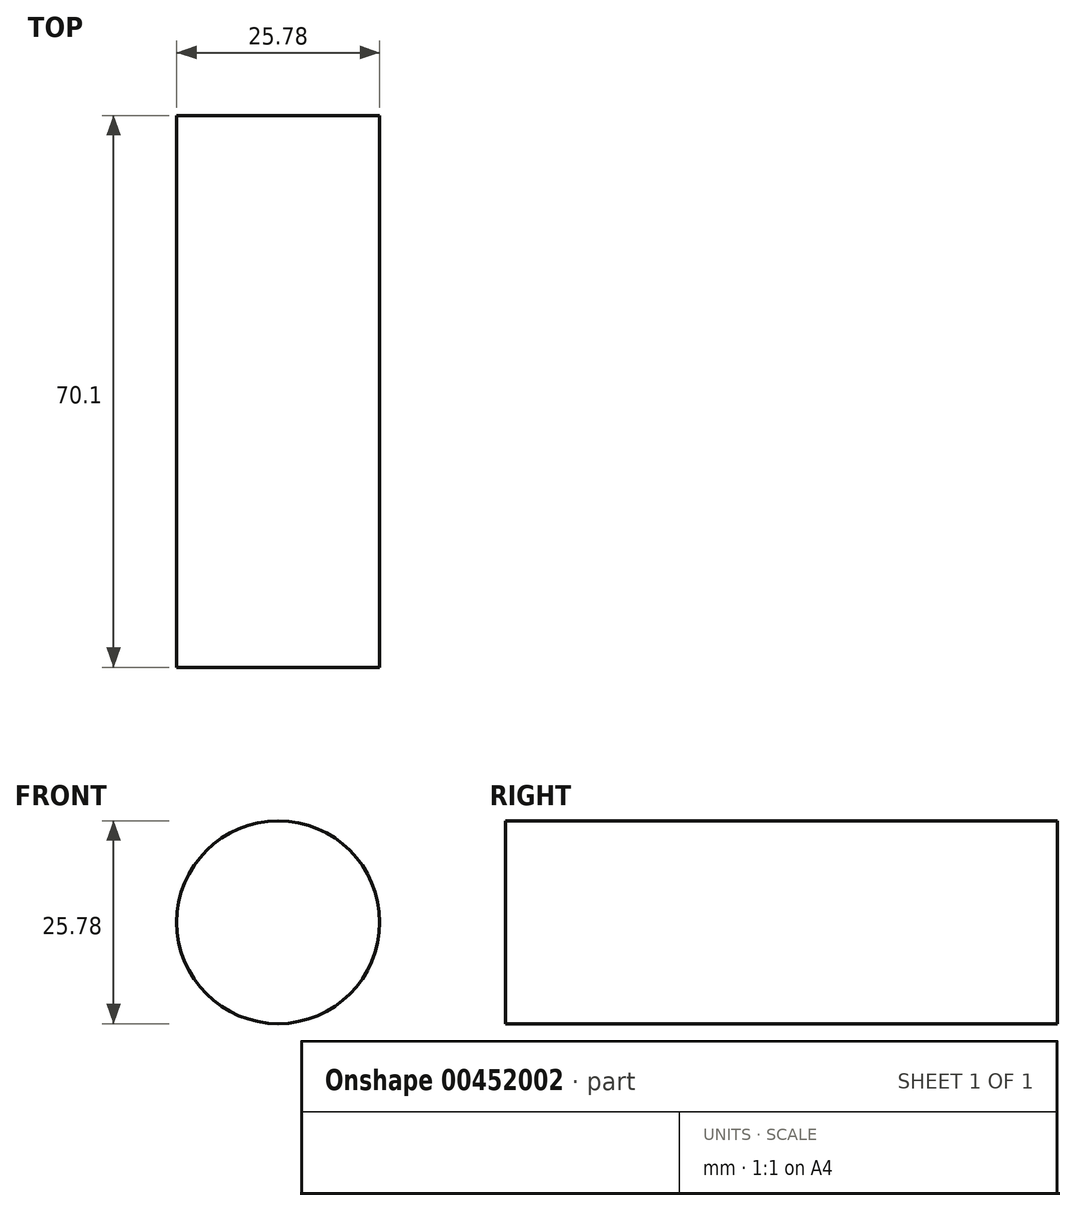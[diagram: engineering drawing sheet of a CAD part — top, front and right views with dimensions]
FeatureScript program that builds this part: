
annotation { "Feature Type Name" : "Feature", "Feature Type Description" : "" }
export const myFeature = defineFeature(function(context is Context, id is Id, definition is map)
    precondition{}
    {
        {
            var Q0;
            Q0=qCreatedBy(makeId("Front.planeOp"),FACE);
            var sketch = newSketch(context, id + "F0", { "sketchPlane" : qUnion([Q0])});
            skCircle(sketch, "E0", {"center": v(0, 0) * mm, "radius": 12.89 * mm});
            skSolve(sketch);
        }
        {
            var Q0;
            Q0 = qSketchRegion(id + "F0", true);
            extrude(context, id + "F1", {"entities" : qUnion([Q0]), "oppositeDirection" : true, "depth" : 70.1 * mm});
        }
    });
